# Revit family: Shower_Arm-DXV-Modulus-D35700317_Series
name_source: partatom
category: Plumbing Fixtures
revit_build: Autodesk Revit 2018 (Build: 20170223_1515(x64)
units: mm (PartAtom-declared; Revit-internal decimal feet)

## family parameters
Cut with Voids When Loaded = No
Host = Face
OmniClass Number = 23.45.05.14.17
OmniClass Title = Showers
Part Type = Normal
Room Calculation Point = No
Round Connector Dimension = Use Radius
Shared = Yes

## types (4) — shared parameters
Assembly Code = D2010700
CW Connection = Yes
Default Elevation = 74"
Description = Modulus 12'' Shower Arm
HW Connection = Yes
Height = 2 9/16"
Installation Type = Wall Mounted
Length = 12 5/8"
Manufacturer = DXV
Price = Prices may vary. Please consult Manufacturer Representative for most up-to-date price list.
Product Documentation Link = https://dxv01.blob.core.windows.net
Product Page URL = https://www.dxv.com
Revised Date = 04/05/2021
Tempered Water Connection Diameter = 1/2"
Tempered Water Connection Radius = 1/4"
URL = www.dxv.com
Vent Connection = No
Warranty Documentation Link = https://www.dxv.com
Waste Connection = No
Width = 2 9/16"
zero-valued in all types: CWFU, HWFU, WFU

## per-type parameters (varying)
| type | Finish | Material |
| D35700317.150 | Cast Brass-DXV-150-Platinum_Nickel | Cast Brass-DXV-150-Platinum_Nickel |
| D35700317.100 | Cast Brass-DXV-100-Polished_Chrome | Cast Brass-DXV-100-Polished_Chrome |
| D35700317.144 | Cast Brass-DXV-144-Brushed_Nickel | Cast Brass-DXV-144-Brushed_Nickel |
| D35700317.243 | Cast Brass-DXV-243-Matte_Black | Cast Brass-DXV-243-Matte_Black |

note: column(s) folded — value = type name in every type: Model

## geometry (parser evidence)
native form markers: Sweep x3
no freeform markers — native parametric forms only
